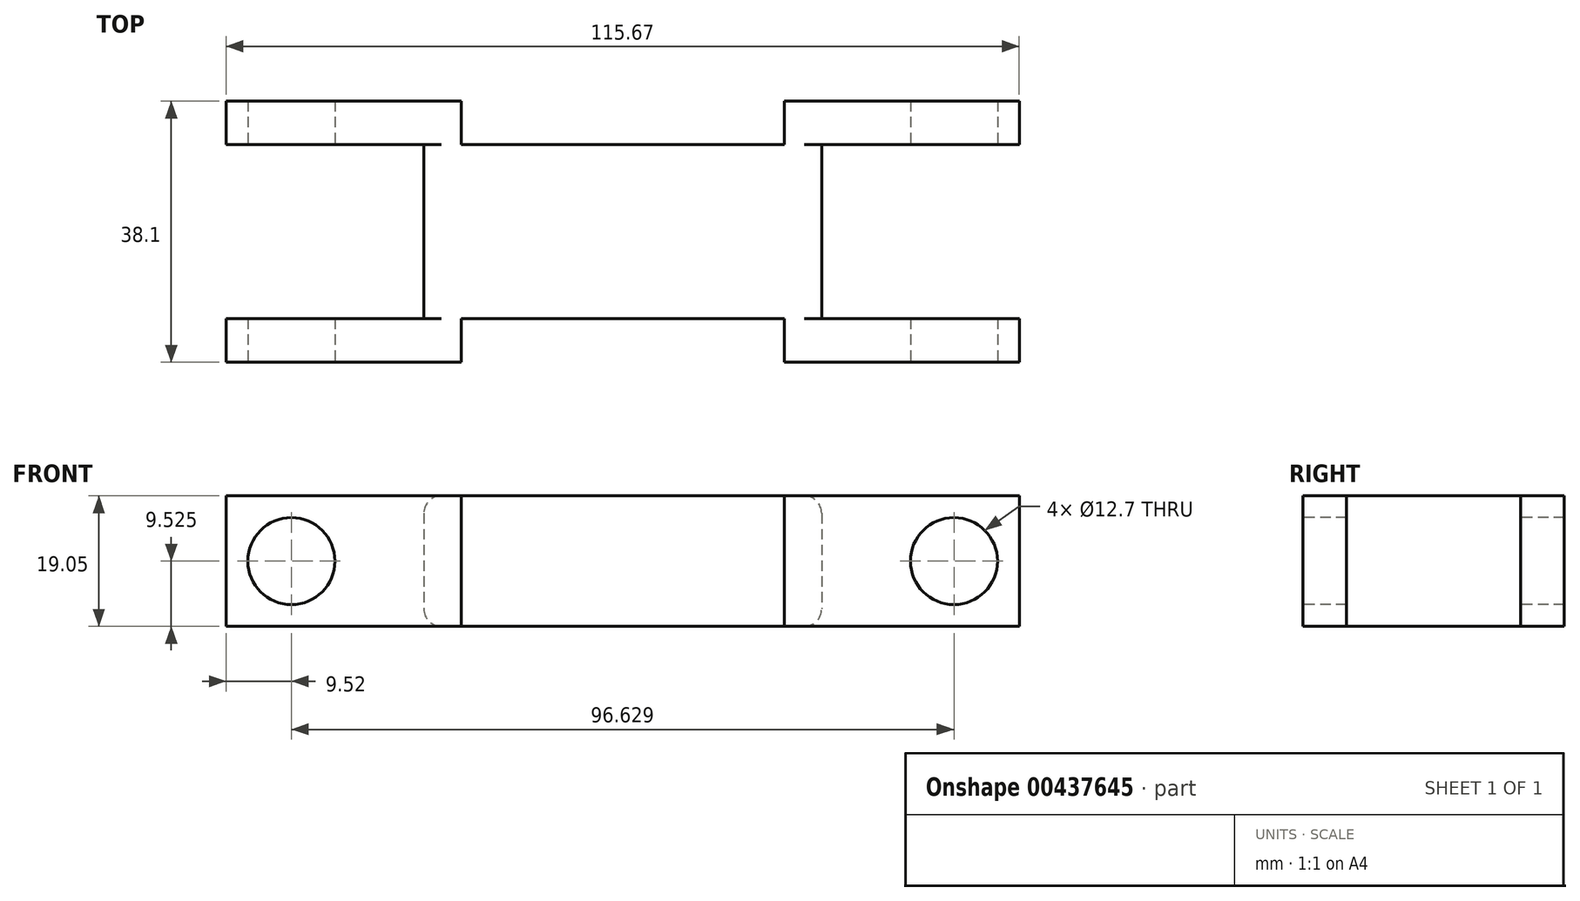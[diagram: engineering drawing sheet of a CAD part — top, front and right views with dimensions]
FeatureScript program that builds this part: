
annotation { "Feature Type Name" : "Feature", "Feature Type Description" : "" }
export const myFeature = defineFeature(function(context is Context, id is Id, definition is map)
    precondition{}
    {
        {
            var Q0;
            Q0=qCreatedBy(makeId("Top.planeOp"),FACE);
            var sketch = newSketch(context, id + "F0", { "sketchPlane" : qUnion([Q0])});
            skLineSegment(sketch, "E0.bottom", {"start": v(-1.7, 2.31) * mm, "end": v(45.4, 2.31) * mm});
            skLineSegment(sketch, "E0.top", {"start": v(-1.7, -23.09) * mm, "end": v(45.4, -23.09) * mm});
            skLineSegment(sketch, "E0.left", {"start": v(-35.98, 8.66) * mm, "end": v(-35.98, 2.31) * mm});
            skLineSegment(sketch, "E1", {"start": v(-35.98, 8.66) * mm, "end": v(-1.7, 8.66) * mm});
            skLineSegment(sketch, "E2", {"start": v(-35.98, -29.44) * mm, "end": v(-1.7, -29.44) * mm});
            skLineSegment(sketch, "E3", {"start": v(-1.7, -29.44) * mm, "end": v(-1.7, -23.09) * mm});
            skPoint(sketch, "E4.orphan", {"position": v(0, 8.66) * mm});
            skLineSegment(sketch, "E5.trimOffspring", {"start": v(-1.7, 2.31) * mm, "end": v(-1.7, 8.66) * mm});
            skLineSegment(sketch, "E6.bottom", {"start": v(-35.98, 2.31) * mm, "end": v(-7.15, 2.31) * mm});
            skLineSegment(sketch, "E6.top", {"start": v(-35.98, -23.09) * mm, "end": v(-7.15, -23.09) * mm});
            skLineSegment(sketch, "E6.right", {"start": v(-7.15, 2.31) * mm, "end": v(-7.15, -23.09) * mm});
            skLineSegment(sketch, "E7.trimOffspring", {"start": v(-35.98, -23.09) * mm, "end": v(-35.98, -29.44) * mm});
            skLineSegment(sketch, "E8", {"start": v(45.4, 8.66) * mm, "end": v(45.4, 2.31) * mm});
            skLineSegment(sketch, "E9", {"start": v(45.4, 8.66) * mm, "end": v(79.7, 8.66) * mm});
            skLineSegment(sketch, "E10", {"start": v(79.7, 8.66) * mm, "end": v(79.7, 2.31) * mm});
            skLineSegment(sketch, "E11", {"start": v(79.7, 2.31) * mm, "end": v(50.87, 2.31) * mm});
            skLineSegment(sketch, "E12", {"start": v(50.87, -23.09) * mm, "end": v(79.7, -23.09) * mm});
            skLineSegment(sketch, "E13", {"start": v(79.7, -23.09) * mm, "end": v(79.7, -29.44) * mm});
            skLineSegment(sketch, "E14", {"start": v(79.7, -29.44) * mm, "end": v(45.4, -29.44) * mm});
            skLineSegment(sketch, "E15", {"start": v(45.4, -29.44) * mm, "end": v(45.4, -23.09) * mm});
            skLineSegment(sketch, "E16", {"start": v(50.87, 2.31) * mm, "end": v(50.87, -23.09) * mm});
            skSolve(sketch);
        }
        {
            var Q0;
            Q0=makeQuery(id+"F0.imprint","IMPRINT",FACE,{"disambiguationData":[TD([[makeQuery(id+"F0.imprint","IMPRINT",EDGE,{"derivedFrom":sQuery(id+"F0.wireOp",EDGE,"E0.bottom")}),-1.0]])]});
            extrude(context, id + "F1", {"entities" : qUnion([Q0]), "depth" : 19.05 * mm});
        }
        {
            var Q0;
            Q0=makeQuery(id+"F1.opExtrude","SWEPT_FACE",FACE,{"disambiguationData":[OSD([sQuery(id+"F0.wireOp",EDGE,"E2")])]});
            var sketch = newSketch(context, id + "F2", { "sketchPlane" : qUnion([Q0])});
            skPoint(sketch, "E17", {"position": v(-26.46, 9.53) * mm});
            skSolve(sketch);
        }
        {
            var Q0;
            Q0=sQuery(id+"F2.wireOp",VERTEX,"E17");
            var Q1;
            Q1=makeQuery(id+"F1.opExtrude","SWEPT_BODY",BODY,{"disambiguationData":[OSD([sQuery(id+"F0.wireOp",EDGE,"E0.bottom"),sQuery(id+"F0.wireOp",EDGE,"E0.top"),sQuery(id+"F0.wireOp",EDGE,"E0.left"),sQuery(id+"F0.wireOp",EDGE,"E0.right"),sQuery(id+"F0.wireOp",EDGE,"E1"),sQuery(id+"F0.wireOp",EDGE,"E2"),sQuery(id+"F0.wireOp",EDGE,"E3"),sQuery(id+"F0.wireOp",EDGE,"E5.trimOffspring"),sQuery(id+"F0.wireOp",EDGE,"E6.bottom"),sQuery(id+"F0.wireOp",EDGE,"E6.top"),sQuery(id+"F0.wireOp",EDGE,"E6.right"),sQuery(id+"F0.wireOp",EDGE,"E7.trimOffspring")])]});
            hole(context, id + "F3", {"style" : HoleStyle.SIMPLE, "endStyle" : HoleEndStyle.THROUGH, "holeDiameter" : 12.7 * mm, "isTappedThrough" : true, "tappedDepth" : 12.7 * mm, "tapClearance" : 3, "locations" : qUnion([Q0]), "scope" : qUnion([Q1])});
        }
        {
            var Q0;
            Q0=makeQuery(id+"F1.opExtrude","SWEPT_FACE",FACE,{"disambiguationData":[OSD([sQuery(id+"F0.wireOp",EDGE,"E14")])]});
            var sketch = newSketch(context, id + "F4", { "sketchPlane" : qUnion([Q0])});
            skLineSegment(sketch, "E18.bottom", {"start": v(79.7, 19.05) * mm, "end": v(70.17, 19.05) * mm});
            skLineSegment(sketch, "E18.top", {"start": v(79.7, 9.53) * mm, "end": v(70.17, 9.52) * mm});
            skLineSegment(sketch, "E18.left", {"start": v(79.7, 19.05) * mm, "end": v(79.7, 9.52) * mm});
            skLineSegment(sketch, "E18.right", {"start": v(70.17, 19.05) * mm, "end": v(70.17, 9.52) * mm});
            skSolve(sketch);
        }
        {
            var Q0;
            Q0=sQuery(id+"F4.wireOp",VERTEX,"E18.right.end");
            var Q1;
            Q1=makeQuery(id+"F1.opExtrude","SWEPT_BODY",BODY,{"disambiguationData":[OSD([sQuery(id+"F0.wireOp",EDGE,"E0.bottom"),sQuery(id+"F0.wireOp",EDGE,"E0.top"),sQuery(id+"F0.wireOp",EDGE,"E0.left"),sQuery(id+"F0.wireOp",EDGE,"E1"),sQuery(id+"F0.wireOp",EDGE,"E2"),sQuery(id+"F0.wireOp",EDGE,"E3"),sQuery(id+"F0.wireOp",EDGE,"E5.trimOffspring"),sQuery(id+"F0.wireOp",EDGE,"E6.bottom"),sQuery(id+"F0.wireOp",EDGE,"E6.top"),sQuery(id+"F0.wireOp",EDGE,"E6.right"),sQuery(id+"F0.wireOp",EDGE,"E7.trimOffspring"),sQuery(id+"F0.wireOp",EDGE,"E8"),sQuery(id+"F0.wireOp",EDGE,"E9"),sQuery(id+"F0.wireOp",EDGE,"E10"),sQuery(id+"F0.wireOp",EDGE,"E11"),sQuery(id+"F0.wireOp",EDGE,"E12"),sQuery(id+"F0.wireOp",EDGE,"E13"),sQuery(id+"F0.wireOp",EDGE,"E14"),sQuery(id+"F0.wireOp",EDGE,"E15"),sQuery(id+"F0.wireOp",EDGE,"E16")])]});
            hole(context, id + "F5", {"style" : HoleStyle.SIMPLE, "endStyle" : HoleEndStyle.THROUGH, "holeDiameter" : 12.7 * mm, "isTappedThrough" : true, "tappedDepth" : 12.7 * mm, "tapClearance" : 3, "startFromSketch" : true, "locations" : qUnion([Q0]), "scope" : qUnion([Q1])});
        }
        {
            var Q0;
            Q0=makeQuery(id+"F1.opExtrude","CAP_EDGE",EDGE,{"disambiguationData":[OSD([sQuery(id+"F0.wireOp",EDGE,"E16")])],"isStart":false});
            var Q1;
            Q1=makeQuery(id+"F1.opExtrude","CAP_EDGE",EDGE,{"disambiguationData":[OSD([sQuery(id+"F0.wireOp",EDGE,"E16")])],"isStart":true});
            var Q2;
            Q2=makeQuery(id+"F1.opExtrude","CAP_EDGE",EDGE,{"disambiguationData":[OSD([sQuery(id+"F0.wireOp",EDGE,"E6.right")])],"isStart":false});
            var Q3;
            Q3=makeQuery(id+"F1.opExtrude","CAP_EDGE",EDGE,{"disambiguationData":[OSD([sQuery(id+"F0.wireOp",EDGE,"E6.right")])],"isStart":true});
            fillet(context, id + "F6", {"entities" : qUnion([Q0, Q1, Q2, Q3]), "radius" : 2.54 * mm, "tangentPropagation" : true, "allowEdgeOverflow" : false});
        }
    });
